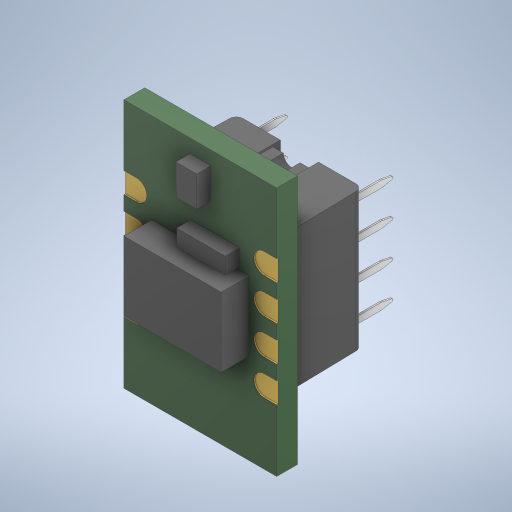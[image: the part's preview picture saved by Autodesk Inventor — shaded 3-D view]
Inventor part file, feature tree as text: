
AUTODESK INVENTOR PART (.ipt)
format: ipt  version: 2024.1 (Build 281209000, 209)  size: 1,565,696 bytes
history: native  units: mm
features: extrude x5, sketch x4, other x1, imported_body x1
ambient origin geometry x8: Origin, YZ Plane, XZ Plane, XY Plane, X Axis, Y Axis, Z Axis, Center Point
bodies: Body1 (feature_tree)
feature tree (11):
  other  "ソリッド1"
  extrude  "押し出し1"  Depth=1.5mm TaperAngle=0.0deg
  extrude  "押し出し2"  Depth=11.0mm
  sketch  "スケッチ3"
  extrude  "押し出し3"  Depth=18.0mm
  extrude  "押し出し4"  Depth=1.5mm TaperAngle=0.0deg
  extrude  "押し出し5"  Depth=2.0mm
  sketch  "スケッチ1"
  sketch  "スケッチ2"
  sketch  "スケッチ4"
  imported_body  "Base1"
